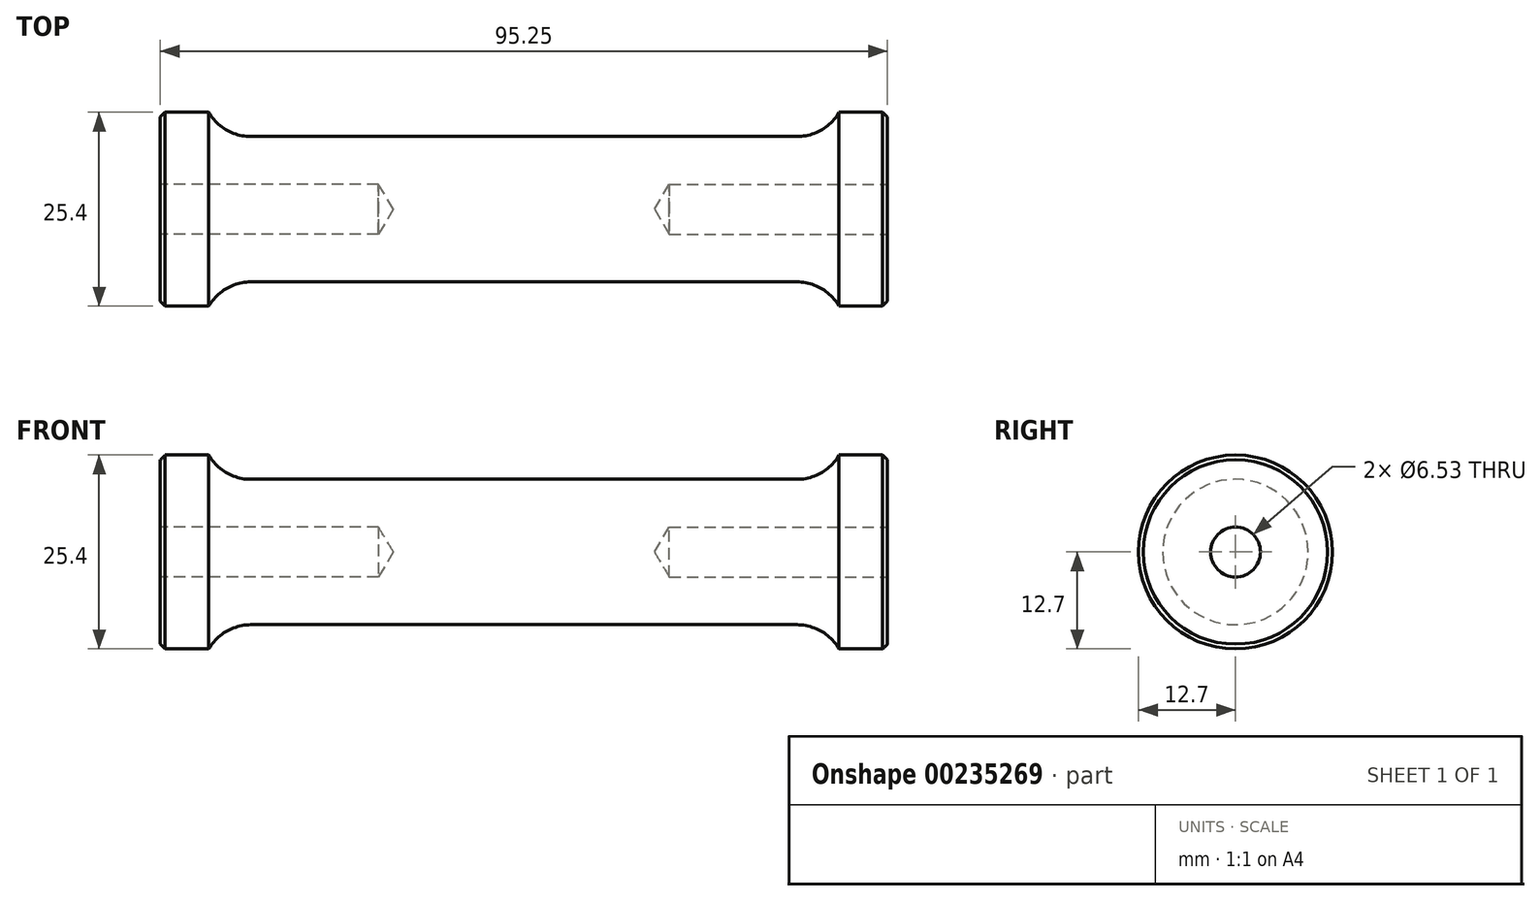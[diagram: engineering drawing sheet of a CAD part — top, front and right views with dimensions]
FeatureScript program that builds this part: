
annotation { "Feature Type Name" : "Feature", "Feature Type Description" : "" }
export const myFeature = defineFeature(function(context is Context, id is Id, definition is map)
    precondition{}
    {
        {
            var Q0;
            Q0=qCreatedBy(makeId("Front.planeOp"),FACE);
            var sketch = newSketch(context, id + "F0", { "sketchPlane" : qUnion([Q0])});
            skLineSegment(sketch, "E0", {"start": v(0, 0) * mm, "end": v(-101.14, 0) * mm, "construction": true});
            skLineSegment(sketch, "E1", {"start": v(0, 0) * mm, "end": v(0, 12.7) * mm});
            skLineSegment(sketch, "E2", {"start": v(0, 12.7) * mm, "end": v(-6.35, 12.7) * mm});
            skLineSegment(sketch, "E3", {"start": v(-11.85, 9.52) * mm, "end": v(-83.4, 9.53) * mm});
            skLineSegment(sketch, "E4", {"start": v(-88.9, 12.7) * mm, "end": v(-95.25, 12.7) * mm});
            skLineSegment(sketch, "E5", {"start": v(-95.25, 12.7) * mm, "end": v(-95.25, 0) * mm});
            skLineSegment(sketch, "E6", {"start": v(8.13, 0) * mm, "end": v(-95.25, 0) * mm});
            skArc(sketch, "E7", {"start": v(-11.85, 9.53) * mm, "mid": v(-8.67, 10.38) * mm, "end": v(-6.35, 12.7) * mm});
            skArc(sketch, "E8", {"start": v(-83.4, 9.52) * mm, "mid": v(-86.58, 10.38) * mm, "end": v(-88.9, 12.7) * mm});
            skSolve(sketch);
        }
        {
            var Q0;
            {var subQ0=sQuery(id+"F0.wireOp",EDGE,"E1");Q0=makeQuery(id+"F0.imprint","IMPRINT",FACE,{"disambiguationData":[TD([[makeQuery(id+"F0.imprint","IMPRINT",EDGE,{"derivedFrom":subQ0}),1.0]])]});}
            var Q1;
            Q1=sQuery(id+"F0.wireOp",EDGE,"E0");
            revolve(context, id + "F1", {"entities" : qUnion([Q0]), "axis" : qUnion([Q1]), "revolveType" : RevolveType.FULL});
        }
        {
            var Q0;
            Q0=makeQuery(id+"F1.opRevolve","SWEPT_FACE",FACE,{"disambiguationData":[OSD([sQuery(id+"F0.wireOp",EDGE,"E1")])]});
            var sketch = newSketch(context, id + "F2", { "sketchPlane" : qUnion([Q0])});
            skCircle(sketch, "E9", {"center": v(0, 0) * mm, "radius": 3.26 * mm});
            skSolve(sketch);
        }
        {
            var Q0;
            Q0=sQuery(id+"F2.wireOp",VERTEX,"E9.center");
            var Q1;
            Q1=makeQuery(id+"F1.opRevolve","SWEPT_BODY",BODY,{"disambiguationData":[OSD([sQuery(id+"F0.wireOp",EDGE,"E1"),sQuery(id+"F0.wireOp",EDGE,"E2"),sQuery(id+"F0.wireOp",EDGE,"E3"),sQuery(id+"F0.wireOp",EDGE,"E4"),sQuery(id+"F0.wireOp",EDGE,"E5"),sQuery(id+"F0.wireOp",EDGE,"E6"),sQuery(id+"F0.wireOp",EDGE,"E7"),sQuery(id+"F0.wireOp",EDGE,"E8")])]});
            hole(context, id + "F3", {"style" : HoleStyle.SIMPLE, "endStyle" : HoleEndStyle.BLIND, "standardTappedOrClearance" : lookupTablePath({ "standard" : "ANSI", "engagement" : "75%", "pitch" : "18 tpi", "size" : "5/16", "type" : "Tapped" }), "standardBlindInLast" : lookupTablePath({ "standard" : "ANSI", "engagement" : "75%", "pitch" : "18 tpi", "size" : "5/16", "type" : "Tapped" }), "holeDiameter" : 6.53 * mm, "holeDepth" : 28.57 * mm, "locations" : qUnion([Q0]), "scope" : qUnion([Q1]), "majorDiameter" : 7.94 * mm});
        }
        {
            var Q0;
            Q0=makeQuery(id+"F1.opRevolve","SWEPT_FACE",FACE,{"disambiguationData":[OSD([sQuery(id+"F0.wireOp",EDGE,"E5")])]});
            var sketch = newSketch(context, id + "F4", { "sketchPlane" : qUnion([Q0])});
            skCircle(sketch, "E10", {"center": v(0, 0) * mm, "radius": 3.26 * mm});
            skSolve(sketch);
        }
        {
            var Q0;
            Q0=sQuery(id+"F4.wireOp",VERTEX,"E10.center");
            var Q1;
            Q1=makeQuery(id+"F1.opRevolve","SWEPT_BODY",BODY,{"disambiguationData":[OSD([sQuery(id+"F0.wireOp",EDGE,"E1"),sQuery(id+"F0.wireOp",EDGE,"E2"),sQuery(id+"F0.wireOp",EDGE,"E3"),sQuery(id+"F0.wireOp",EDGE,"E4"),sQuery(id+"F0.wireOp",EDGE,"E5"),sQuery(id+"F0.wireOp",EDGE,"E6"),sQuery(id+"F0.wireOp",EDGE,"E7"),sQuery(id+"F0.wireOp",EDGE,"E8")])]});
            hole(context, id + "F5", {"style" : HoleStyle.SIMPLE, "endStyle" : HoleEndStyle.BLIND, "standardTappedOrClearance" : lookupTablePath({ "standard" : "ANSI", "engagement" : "75%", "pitch" : "18 tpi", "size" : "5/16", "type" : "Tapped" }), "standardBlindInLast" : lookupTablePath({ "standard" : "ANSI", "engagement" : "75%", "pitch" : "18 tpi", "size" : "5/16", "type" : "Tapped" }), "holeDiameter" : 6.53 * mm, "holeDepth" : 28.57 * mm, "locations" : qUnion([Q0]), "scope" : qUnion([Q1]), "majorDiameter" : 7.94 * mm});
        }
        {
            var Q0;
            Q0=makeQuery(id+"F1.opRevolve","SWEPT_EDGE",EDGE,{"disambiguationData":[OSD([sQuery(id+"F0.wireOp",EDGE,"E1"),sQuery(id+"F0.wireOp",EDGE,"E2")])]});
            var Q1;
            Q1=makeQuery(id+"F1.opRevolve","SWEPT_EDGE",EDGE,{"disambiguationData":[OSD([sQuery(id+"F0.wireOp",EDGE,"E4"),sQuery(id+"F0.wireOp",EDGE,"E5")])]});
            chamfer(context, id + "F6", {"entities" : qUnion([Q0, Q1]), "width" : 0.64 * mm, "tangentPropagation" : true});
        }
    });
